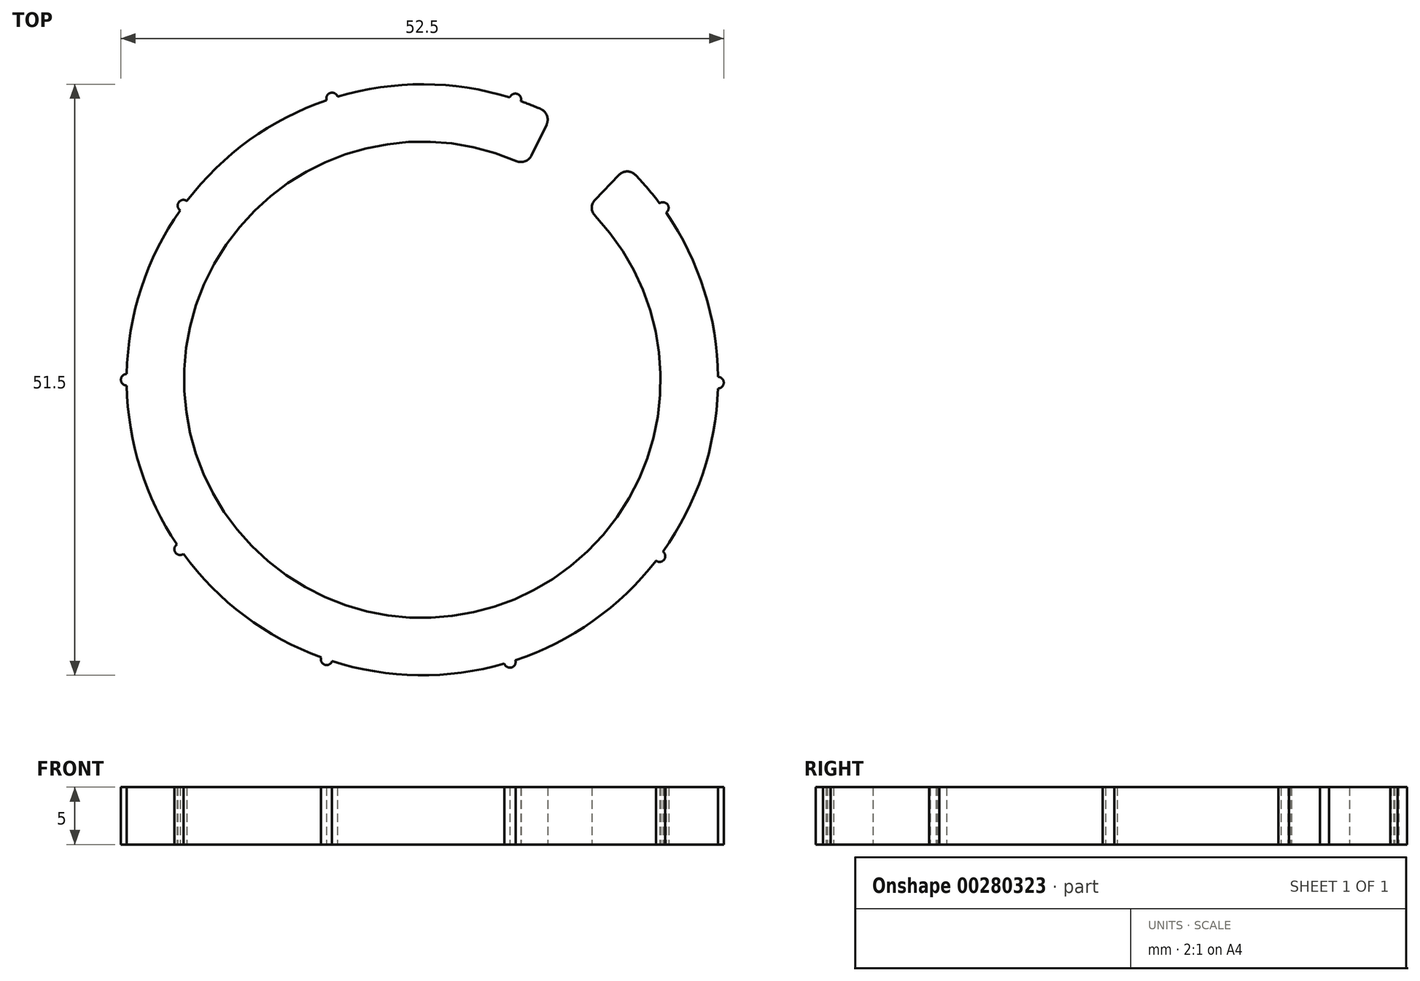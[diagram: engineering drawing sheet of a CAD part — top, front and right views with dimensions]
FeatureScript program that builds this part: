
annotation { "Feature Type Name" : "Feature", "Feature Type Description" : "" }
export const myFeature = defineFeature(function(context is Context, id is Id, definition is map)
    precondition{}
    {
        {
            var Q0;
            Q0=qCreatedBy(makeId("Top.planeOp"),FACE);
            var sketch = newSketch(context, id + "F0", { "sketchPlane" : qUnion([Q0])});
            skArc(sketch, "E0", {"start": v(11.26, 23.16) * mm, "mid": v(-14.72, -21.13) * mm, "end": v(17.82, 18.58) * mm});
            skArc(sketch, "E1", {"start": v(9.07, 18.66) * mm, "mid": v(-11.86, -17.02) * mm, "end": v(14.36, 14.98) * mm});
            skLineSegment(sketch, "E2", {"start": v(9.07, 18.66) * mm, "end": v(11.26, 23.16) * mm});
            skLineSegment(sketch, "E3", {"start": v(14.36, 14.98) * mm, "end": v(17.82, 18.58) * mm});
            skCircle(sketch, "E4", {"center": v(-25.75, 0) * mm, "radius": 0.5 * mm});
            skCircle(sketch, "E5.1.0", {"center": v(-20.8, 15.18) * mm, "radius": 0.5 * mm});
            skCircle(sketch, "E5.2.0", {"center": v(-7.86, 24.52) * mm, "radius": 0.5 * mm});
            skCircle(sketch, "E5.3.0", {"center": v(8.1, 24.44) * mm, "radius": 0.5 * mm});
            skCircle(sketch, "E5.4.0", {"center": v(20.95, 14.97) * mm, "radius": 0.5 * mm});
            skCircle(sketch, "E5.5.0", {"center": v(25.75, -0.25) * mm, "radius": 0.5 * mm});
            skCircle(sketch, "E5.6.0", {"center": v(20.65, -15.38) * mm, "radius": 0.5 * mm});
            skCircle(sketch, "E5.7.0", {"center": v(7.62, -24.6) * mm, "radius": 0.5 * mm});
            skCircle(sketch, "E5.8.0", {"center": v(-8.34, -24.36) * mm, "radius": 0.5 * mm});
            skCircle(sketch, "E5.9.0", {"center": v(-21.1, -14.77) * mm, "radius": 0.5 * mm});
            skLineSegment(sketch, "E5.anchor1", {"start": v(0, 0) * mm, "end": v(-25.75, 0) * mm, "construction": true});
            skLineSegment(sketch, "E5.anchor2", {"start": v(0, 0) * mm, "end": v(-21.1, -14.77) * mm, "construction": true});
            skSolve(sketch);
        }
        {
            var Q0;
            Q0 = qSketchRegion(id + "F0", true);
            extrude(context, id + "F1", {"entities" : qUnion([Q0]), "depth" : 5 * mm});
        }
        {
            var Q0;
            Q0=makeQuery(id+"F1.opExtrude","SWEPT_EDGE",EDGE,{"disambiguationData":[OSD([sQuery(id+"F0.wireOp",EDGE,"E1"),sQuery(id+"F0.wireOp",EDGE,"E2")])]});
            var Q1;
            Q1=makeQuery(id+"F1.opExtrude","SWEPT_EDGE",EDGE,{"disambiguationData":[OSD([sQuery(id+"F0.wireOp",EDGE,"E0"),sQuery(id+"F0.wireOp",EDGE,"E2")])]});
            var Q2;
            Q2=makeQuery(id+"F1.opExtrude","SWEPT_EDGE",EDGE,{"disambiguationData":[OSD([sQuery(id+"F0.wireOp",EDGE,"E0"),sQuery(id+"F0.wireOp",EDGE,"E3")])]});
            var Q3;
            Q3=makeQuery(id+"F1.opExtrude","SWEPT_EDGE",EDGE,{"disambiguationData":[OSD([sQuery(id+"F0.wireOp",EDGE,"E1"),sQuery(id+"F0.wireOp",EDGE,"E3")])]});
            fillet(context, id + "F2", {"entities" : qUnion([Q0, Q1, Q2, Q3]), "radius" : 1 * mm, "tangentPropagation" : true, "allowEdgeOverflow" : false});
        }
    });
